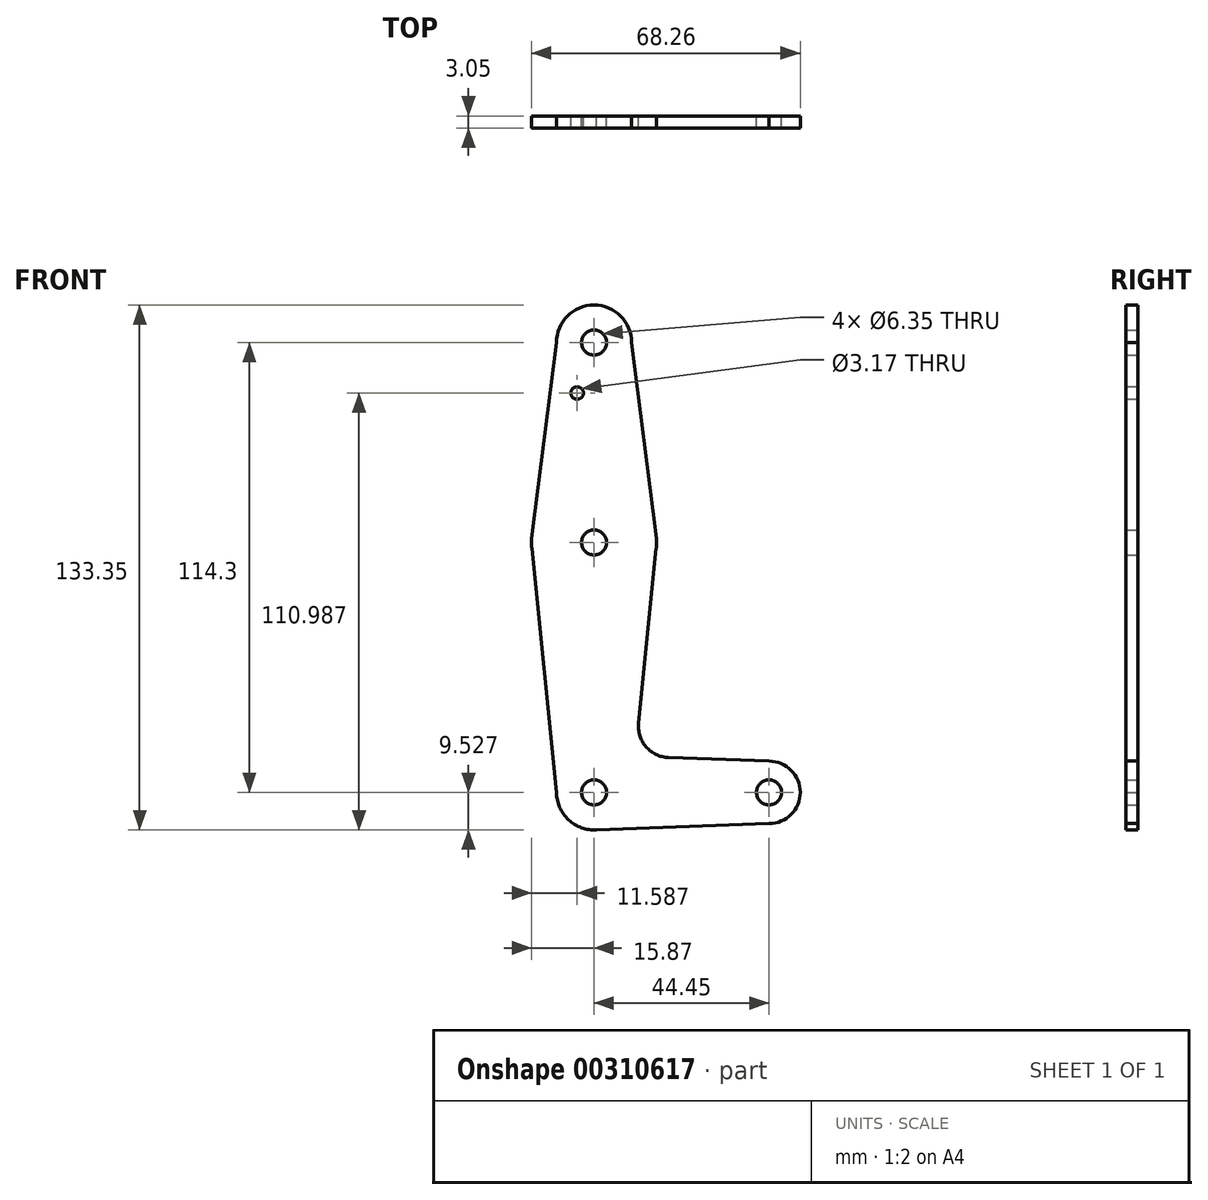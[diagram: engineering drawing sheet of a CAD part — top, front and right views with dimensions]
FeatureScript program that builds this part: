
annotation { "Feature Type Name" : "Feature", "Feature Type Description" : "" }
export const myFeature = defineFeature(function(context is Context, id is Id, definition is map)
    precondition{}
    {
        {
            var Q0;
            Q0=qCreatedBy(makeId("Front.planeOp"),FACE);
            var sketch = newSketch(context, id + "F0", { "sketchPlane" : qUnion([Q0])});
            skCircle(sketch, "E0", {"center": v(-33.83, 68.43) * mm, "radius": 9.53 * mm});
            skCircle(sketch, "E1", {"center": v(-33.83, -45.87) * mm, "radius": 9.53 * mm});
            skCircle(sketch, "E2", {"center": v(-33.83, 17.63) * mm, "radius": 15.88 * mm});
            skLineSegment(sketch, "E3", {"start": v(-24.3, 68.43) * mm, "end": v(-18.08, 19.63) * mm});
            skLineSegment(sketch, "E4.MirrorCS", {"start": v(-43.35, 68.43) * mm, "end": v(-49.58, 19.63) * mm});
            skLineSegment(sketch, "E5", {"start": v(-43.35, -45.87) * mm, "end": v(-49.62, 16.03) * mm});
            skLineSegment(sketch, "E6.MirrorCS", {"start": v(-22.52, -28.28) * mm, "end": v(-18.04, 16.03) * mm});
            skCircle(sketch, "E7", {"center": v(10.62, -45.87) * mm, "radius": 7.94 * mm});
            skCircle(sketch, "E8", {"center": v(-33.83, 68.43) * mm, "radius": 3.18 * mm});
            skCircle(sketch, "E9", {"center": v(-33.83, 17.63) * mm, "radius": 3.18 * mm});
            skCircle(sketch, "E10", {"center": v(-33.83, -45.87) * mm, "radius": 3.18 * mm});
            skCircle(sketch, "E11", {"center": v(10.62, -45.87) * mm, "radius": 3.18 * mm});
            skCircle(sketch, "E12", {"center": v(-38.11, 55.59) * mm, "radius": 1.59 * mm});
            skLineSegment(sketch, "E13", {"start": v(-33.83, -55.4) * mm, "end": v(10.62, -53.81) * mm});
            skLineSegment(sketch, "E14.MirrorCS", {"start": v(-14.9, -37.02) * mm, "end": v(10.62, -37.94) * mm});
            skPoint(sketch, "E15.newPointA", {"position": v(-24.3, -45.87) * mm});
            skPoint(sketch, "E15.newPointB", {"position": v(-33.83, -36.35) * mm});
            skArc(sketch, "E15.filletArc", {"start": v(-22.52, -28.28) * mm, "mid": v(-20.6, -34.3) * mm, "end": v(-14.9, -37.02) * mm});
            skSolve(sketch);
        }
        {
            var Q0;
            Q0 = qSketchRegion(id + "F0", true);
            extrude(context, id + "F1", {"entities" : qUnion([Q0]), "depth" : 3.05 * mm});
        }
    });
